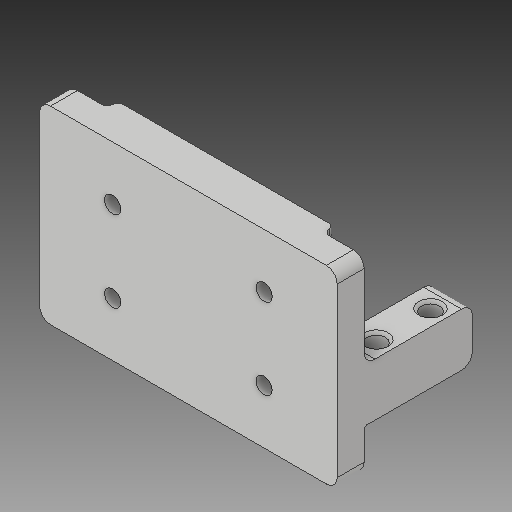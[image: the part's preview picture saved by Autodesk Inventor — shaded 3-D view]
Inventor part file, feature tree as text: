
AUTODESK INVENTOR PART (.ipt)
format: ipt  version: 2019 (Build 230136000, 136)  size: 176,640 bytes
history: native  units: mm
features: sketch x4, other x3
ambient origin geometry x8: Origin, YZ Plane, XZ Plane, XY Plane, X Axis, Y Axis, Z Axis, Center Point
bodies: Solid1 (feature_tree)
feature tree (7):
  other  "big_servo_hold.ipt"
  other  "Solid1::big_servo_hold.ipt"
  other  "TaggingFeature1"
  sketch  "Sketch1"  dims[d0=10.0mm]
  sketch  "Sketch2"
  sketch  "Sketch3"
  sketch  "Sketch4"
